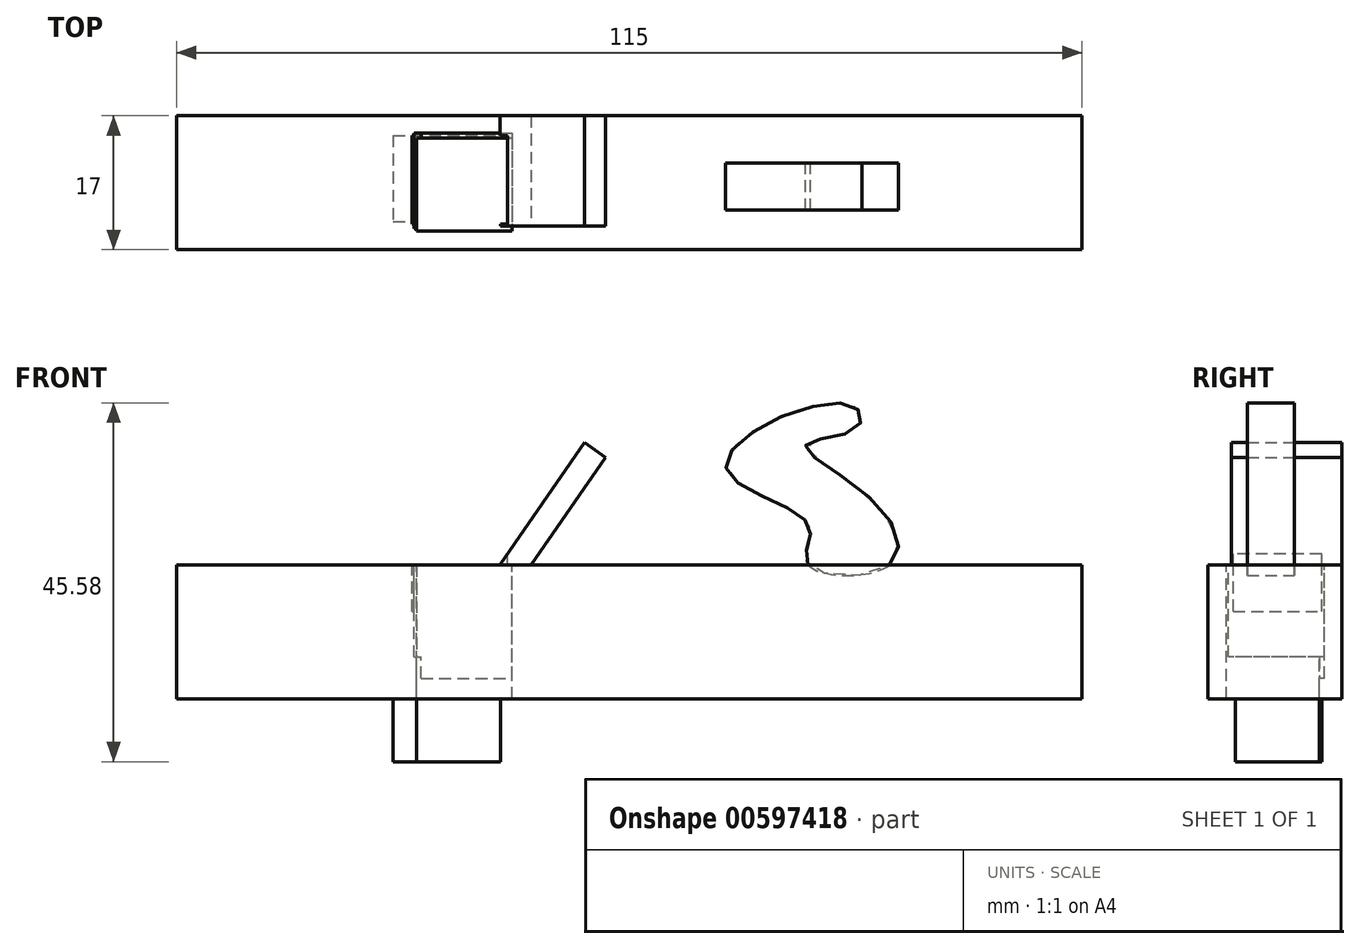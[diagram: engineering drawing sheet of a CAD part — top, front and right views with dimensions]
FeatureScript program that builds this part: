
annotation { "Feature Type Name" : "Feature", "Feature Type Description" : "" }
export const myFeature = defineFeature(function(context is Context, id is Id, definition is map)
    precondition{}
    {
        {
            var Q0;
            Q0=qCreatedBy(makeId("Front.planeOp"),FACE);
            var sketch = newSketch(context, id + "F0", { "sketchPlane" : qUnion([Q0])});
            skLineSegment(sketch, "E0.bottom", {"start": v(-86.33, 0) * mm, "end": v(28.67, 0) * mm});
            skLineSegment(sketch, "E0.top", {"start": v(-86.33, -17) * mm, "end": v(28.67, -17) * mm});
            skLineSegment(sketch, "E0.left", {"start": v(-86.33, 0) * mm, "end": v(-86.33, -17) * mm});
            skLineSegment(sketch, "E0.right", {"start": v(28.67, 0) * mm, "end": v(28.67, -17) * mm});
            skLineSegment(sketch, "E1.0", {"start": v(-56.33, 0) * mm, "end": v(-56.33, -17) * mm, "construction": true});
            skLineSegment(sketch, "E2", {"start": v(-39.23, 0) * mm, "end": v(-52.85, -17) * mm, "construction": true});
            skSolve(sketch);
        }
        {
            var Q0;
            Q0=qCreatedBy(makeId("Front.planeOp"),FACE);
            var sketch = newSketch(context, id + "F1", { "sketchPlane" : qUnion([Q0])});
            skLineSegment(sketch, "E3", {"start": v(-54.37, -13.17) * mm, "end": v(-34.53, 15.54) * mm});
            skLineSegment(sketch, "E4", {"start": v(-34.53, 15.54) * mm, "end": v(-31.84, 13.68) * mm});
            skLineSegment(sketch, "E5", {"start": v(-31.84, 13.68) * mm, "end": v(-50, -12.62) * mm});
            skLineSegment(sketch, "E6", {"start": v(-50, -12.62) * mm, "end": v(-54.37, -13.17) * mm});
            skSolve(sketch);
        }
        {
            var Q0;
            Q0=qCreatedBy(makeId("Front.planeOp"),FACE);
            cPlane(context, id + "F2", {"entities" : qUnion([Q0]), "cplaneType" : CPlaneType.OFFSET, "offset" : 6 * mm, "width" : 150 * mm, "height" : 150 * mm});
        }
        {
            var Q0;
            Q0=qCreatedBy(id+"F2.planeOp",FACE);
            var sketch = newSketch(context, id + "F3", { "sketchPlane" : qUnion([Q0])});
            skFitSpline(sketch, "E7", {"points": [v(4.25, 0) * mm, v(2.47, 7.85) * mm, v(-6.4, 15.25) * mm, v(0, 17.32) * mm, v(0, 19.98) * mm, v(-10.85, 18.2) * mm, v(-16.47, 12) * mm, v(-8.18, 6.96) * mm, v(-5.82, 3.7) * mm, v(-6.11, 0) * mm, v(4.25, 0) * mm]});
            skSolve(sketch);
        }
        {
            var Q0;
            Q0 = qSketchRegion(id + "F3", true);
            extrude(context, id + "F4", {"entities" : qUnion([Q0]), "depth" : 6 * mm, "offsetDistance" : 25 * mm});
        }
        {
            var Q0;
            Q0 = qSketchRegion(id + "F1", true);
            extrude(context, id + "F5", {"entities" : qUnion([Q0]), "operationType" : NewBodyOperationType.ADD, "depth" : 14 * mm, "offsetDistance" : 25 * mm});
        }
        {
            var Q0;
            Q0 = qSketchRegion(id + "F1", true);
            extrude(context, id + "F6", {"entities" : qUnion([Q0]), "depth" : 14 * mm, "offsetDistance" : 25 * mm});
        }
        {
            var Q0;
            Q0 = qSketchRegion(id + "F0", true);
            extrude(context, id + "F7", {"entities" : qUnion([Q0]), "depth" : 17 * mm, "offsetDistance" : 25 * mm});
        }
        {
            var Q0;
            Q0=qCreatedBy(makeId("Top.planeOp"),FACE);
            var sketch = newSketch(context, id + "F8", { "sketchPlane" : qUnion([Q0])});
            skLineSegment(sketch, "E8.bottom", {"start": v(-58.51, -2.22) * mm, "end": v(-45.49, -2.22) * mm});
            skLineSegment(sketch, "E8.top", {"start": v(-58.51, -13.47) * mm, "end": v(-45.49, -13.47) * mm});
            skLineSegment(sketch, "E8.left", {"start": v(-58.51, -2.22) * mm, "end": v(-58.51, -13.47) * mm});
            skLineSegment(sketch, "E8.right", {"start": v(-45.49, -2.22) * mm, "end": v(-45.49, -13.47) * mm});
            skSolve(sketch);
        }
        {
            var Q0;
            Q0 = qSketchRegion(id + "F8", true);
            extrude(context, id + "F9", {"entities" : qUnion([Q0]), "operationType" : NewBodyOperationType.REMOVE, "oppositeDirection" : true, "depth" : -20 * mm, "offsetDistance" : 25 * mm});
        }
        {
            var Q0;
            Q0=qCreatedBy(makeId("Top.planeOp"),FACE);
            var sketch = newSketch(context, id + "F10", { "sketchPlane" : qUnion([Q0])});
            skLineSegment(sketch, "E9.bottom", {"start": v(-58.8, -2.52) * mm, "end": v(-45.2, -2.52) * mm});
            skLineSegment(sketch, "E9.top", {"start": v(-58.8, -13.47) * mm, "end": v(-45.2, -13.47) * mm});
            skLineSegment(sketch, "E9.left", {"start": v(-58.8, -2.52) * mm, "end": v(-58.8, -13.47) * mm});
            skLineSegment(sketch, "E9.right", {"start": v(-45.2, -2.52) * mm, "end": v(-45.2, -13.47) * mm});
            skSolve(sketch);
        }
        {
            var Q0;
            Q0 = qSketchRegion(id + "F10", true);
            extrude(context, id + "F11", {"entities" : qUnion([Q0]), "operationType" : NewBodyOperationType.ADD, "oppositeDirection" : true, "depth" : 25 * mm, "offsetDistance" : 25 * mm});
        }
        {
            var Q0;
            Q0=qCreatedBy(makeId("Top.planeOp"),FACE);
            var sketch = newSketch(context, id + "F12", { "sketchPlane" : qUnion([Q0])});
            skLineSegment(sketch, "E10.bottom", {"start": v(-56.14, -2.22) * mm, "end": v(-44.9, -2.22) * mm});
            skLineSegment(sketch, "E10.top", {"start": v(-56.14, -14.36) * mm, "end": v(-44.9, -14.36) * mm});
            skLineSegment(sketch, "E10.left", {"start": v(-56.14, -2.22) * mm, "end": v(-56.14, -14.36) * mm});
            skLineSegment(sketch, "E10.right", {"start": v(-44.9, -2.22) * mm, "end": v(-44.9, -14.36) * mm});
            skSolve(sketch);
        }
        {
            var Q0;
            Q0 = qSketchRegion(id + "F12", true);
            extrude(context, id + "F13", {"entities" : qUnion([Q0]), "operationType" : NewBodyOperationType.REMOVE, "oppositeDirection" : true, "depth" : 11.7 * mm, "offsetDistance" : 25 * mm});
        }
        {
            var Q0;
            Q0=qCreatedBy(makeId("Top.planeOp"),FACE);
            var sketch = newSketch(context, id + "F14", { "sketchPlane" : qUnion([Q0])});
            skLineSegment(sketch, "E11.bottom", {"start": v(-55.85, -2.81) * mm, "end": v(-43.71, -2.81) * mm});
            skLineSegment(sketch, "E11.top", {"start": v(-55.85, -14.65) * mm, "end": v(-43.71, -14.65) * mm});
            skLineSegment(sketch, "E11.left", {"start": v(-55.85, -2.81) * mm, "end": v(-55.85, -14.65) * mm});
            skLineSegment(sketch, "E11.right", {"start": v(-43.71, -2.81) * mm, "end": v(-43.71, -14.65) * mm});
            skSolve(sketch);
        }
        {
            var Q0;
            Q0 = qSketchRegion(id + "F14", true);
            extrude(context, id + "F15", {"entities" : qUnion([Q0]), "operationType" : NewBodyOperationType.REMOVE, "oppositeDirection" : true, "depth" : 25 * mm, "offsetDistance" : 25 * mm});
        }
        {
            var Q0;
            Q0=qCreatedBy(makeId("Top.planeOp"),FACE);
            var sketch = newSketch(context, id + "F16", { "sketchPlane" : qUnion([Q0])});
            skLineSegment(sketch, "E12.bottom", {"start": v(-55.26, -2.22) * mm, "end": v(-43.71, -2.22) * mm});
            skLineSegment(sketch, "E12.top", {"start": v(-55.26, -14.06) * mm, "end": v(-43.71, -14.06) * mm});
            skLineSegment(sketch, "E12.left", {"start": v(-55.26, -2.22) * mm, "end": v(-55.26, -14.06) * mm});
            skLineSegment(sketch, "E12.right", {"start": v(-43.71, -2.22) * mm, "end": v(-43.71, -14.06) * mm});
            skSolve(sketch);
        }
        {
            var Q0;
            Q0 = qSketchRegion(id + "F16", true);
            extrude(context, id + "F17", {"entities" : qUnion([Q0]), "operationType" : NewBodyOperationType.REMOVE, "oppositeDirection" : true, "depth" : 14.4 * mm, "offsetDistance" : 25 * mm});
        }
        {
            var Q0;
            Q0=qCreatedBy(makeId("Top.planeOp"),FACE);
            cPlane(context, id + "F18", {"entities" : qUnion([Q0]), "cplaneType" : CPlaneType.OFFSET, "offset" : 3 * mm, "width" : 150 * mm, "height" : 150 * mm});
        }
        {
            var Q0;
            Q0=qCreatedBy(id+"F18.planeOp",FACE);
            var sketch = newSketch(context, id + "F19", { "sketchPlane" : qUnion([Q0])});
            skLineSegment(sketch, "E13.bottom", {"start": v(-56.44, -2.52) * mm, "end": v(-44.3, -2.52) * mm});
            skLineSegment(sketch, "E13.top", {"start": v(-56.44, -13.77) * mm, "end": v(-44.3, -13.77) * mm});
            skLineSegment(sketch, "E13.left", {"start": v(-56.44, -2.52) * mm, "end": v(-56.44, -13.77) * mm});
            skLineSegment(sketch, "E13.right", {"start": v(-44.3, -2.52) * mm, "end": v(-44.3, -13.77) * mm});
            skSolve(sketch);
        }
        {
            var Q0;
            Q0 = qSketchRegion(id + "F19", true);
            extrude(context, id + "F20", {"entities" : qUnion([Q0]), "operationType" : NewBodyOperationType.REMOVE, "oppositeDirection" : true, "depth" : 8.9 * mm, "offsetDistance" : 25 * mm});
        }
        {
            var Q0;
            Q0=qCreatedBy(id+"F18.planeOp",FACE);
            var sketch = newSketch(context, id + "F21", { "sketchPlane" : qUnion([Q0])});
            skLineSegment(sketch, "E14.bottom", {"start": v(-55.26, -2.81) * mm, "end": v(-45.2, -2.81) * mm});
            skLineSegment(sketch, "E14.top", {"start": v(-55.26, -14.36) * mm, "end": v(-45.2, -14.36) * mm});
            skLineSegment(sketch, "E14.left", {"start": v(-55.26, -2.81) * mm, "end": v(-55.26, -14.36) * mm});
            skLineSegment(sketch, "E14.right", {"start": v(-45.2, -2.81) * mm, "end": v(-45.2, -14.36) * mm});
            skSolve(sketch);
        }
        {
            var Q0;
            Q0 = qSketchRegion(id + "F21", true);
            extrude(context, id + "F22", {"entities" : qUnion([Q0]), "operationType" : NewBodyOperationType.REMOVE, "oppositeDirection" : true, "depth" : 9.8 * mm, "offsetDistance" : 25 * mm});
        }
    });
